# Revit family: TSM Betonschraube Senkkopf mit Torx-Antrieb, vz  6x 80
name_source: partatom
category: HLS-Bauteile
units: mm (PartAtom-declared; Revit-internal decimal feet)

## family parameters
Arbeitsebenenbasiert = Ja
Beim Laden mit Abzugskörper schneiden = Nein
Bemaßung runder Anschluss = Durchmesser verwenden
Beschriftungsausrichtung beibehalten = Nein
Gemeinsam genutzt = Ja
Immer vertikal = Nein
Raumberechnungspunkt = Nein
Teiletyp = Normal

## types (1)
- TSM Betonschrauben Senkkopf mit TX-Antrieb, vz  6x 80 TX30
    Artikelnummer = 2230681
    Bohrerdurchmesser = 6 mm
    Durchmesser Kopf = 13 mm
    EAN = 4260116911492
    Fabrikat = Toge
    Firma = MEFA Befestigungs- und Montagesysteme GmbH
    Form Kopf = Flachsenkkopf
    Gewicht = 0.02 kg
    Gewicht pro Bauteil = 0.02 kg
    Kurztext1 = Betonschraube TSM 6 TX 30
    Kurztext2 = 6x80 mm Flachsenkkopf 13 mm
    Länge = 80 mm  [stored 0.262467 ft]
    Material = Stahl
    Mengeneinheit = St
    Oberflaeche = galvanisch verzinkt
    Vorgabe-Ansicht = 1219 mm
    max. Klemmstärke = 25 mm  [stored 0.082021 ft]
    min. Bohrlochtiefe = 60 mm
    min. Verankerungstiefe = 55 mm
    vpe = 100

note: [stored X ft] marks values corroborated as IEEE doubles in the binary element streams (Revit-internal decimal feet)
